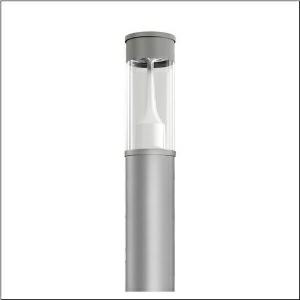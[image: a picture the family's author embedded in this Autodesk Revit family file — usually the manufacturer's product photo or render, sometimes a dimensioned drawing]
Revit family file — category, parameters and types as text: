
# Revit family: city-light_400_iq___st1_2a_5xa5305af14hp_8cfd
name_source: partatom
category: Lighting Fixtures
units: mm (PartAtom-declared; Revit-internal decimal feet)

## family parameters
Cut with Voids When Loaded = No
Host = Face
Light Source = No
Part Type = Normal
Room Calculation Point = No
Round Connector Dimension = Use Diameter
Shared = No

## types (1)
- --- (1 x LED, 3910 lm, 33.6 W, 2200K)
    Apparent Load = 34 VA
    CIE Flux Codes = 22 61 94 96 100
    Color Rendering = 70
    Color Temperature = 2200K
    Default Elevation = 1800 mm
    Description = City-Light 400 iQ, light pillar, Module 540 iQ-SR, primary light control with 3 zone facetted reflector, of plastic, silver coated, highly specular, structured, primary optical cover: cover, of PMMA, transparent, partly coated, light distribution: ST1.2a, primary light characteristic: asymmetric, LED, High Power LED, rated luminous flux: 3.910lm, luminous efficacy: 116lm/W, light colour: 722, colour temperature: 2200K, control gear: iQ Street-Remote, control: pre-setting: logarithmic dimming characteristic, Street-Remote, Auto-Match, Temp-Guard, Lumen-Switch, Night-Set, Smart-Wire, Light-Fading, Desk-Remote (wireless, voltage-free reading and setting of iQ features in the workshop via application-optimized NFC function/RFID function), optimised constant luminous flux control (CLO 2.0), with terminal, 6-pole, max. 2.5mm², mains connection: 230..240V, AC, 50/60Hz, start of lifetime: 34W, end of service life: 36W, reduction: 15W, luminaire housing, cylindrical, of extruded aluminium section, coated, Siteco® metallic grey (DB 702S), length: 4.694mm, diameter: 200mm, Module 540 iQ-SR, traffic white (RAL 9016), equipment: Power, protection rating (complete): IP65, insulation class (complete): insulation class II (safety insulation), certification: CE, ENEC, VDE, packaging unit: 1 piece

Light Distribution: ST1.2a
    Height = 500 mm
    Lamp = 1 x LED
    Lamp Light Flux = 3910 lm
    Lamp Power = 33.6 W
    Lamp count = 1
    Length = 200 mm  [stored 0.656168 ft]
    Luminous efficacy = 116 lm/W
    Manufacturer = Siteco
    ModVariant = No
    Model = 5XA5305AF14HP
    Mounting Place = Floor
    Mounting Type = Freestanding
    Number of Poles = 1
    OnlyDefault = Yes
    Power Factor = 1
    Product Name = City-Light 400 iQ | ST1.2a
    Product group = light pillar
    ProductGroupID = 1301
    Protection Class = Protection class II
    Protection Degree = IP 65
    RLX_Detail_Level = 1
    RLX_Emergency_Light_Flux = 0 lm
    RLX_Emergency_Type = 0
    RLX_Emergency_Type_DB = No
    RlxData = <blob elided: 53397 chars, md5=fabef285>
    Socket = socket
    Standby Power = 0 W
    System Light Flux = 3910 lm
    System Power = 34 W
    Type Comments = factory setting: luminous flux: 100 % | dim-lin: 254 | 695 mA
    Type Image = l_1006916.jpg
    URL = http://relux.com
    VarID = @adj_190363
    Voltage = 0 V
    Weight = 0.00 kg
    Width = 0 mm  [stored 0 ft]

note: [stored X ft] marks values corroborated as IEEE doubles in the binary element streams (Revit-internal decimal feet)

## geometry (parser evidence)
native form markers: Blend x4, Sweep x11
no freeform markers — native parametric forms only
